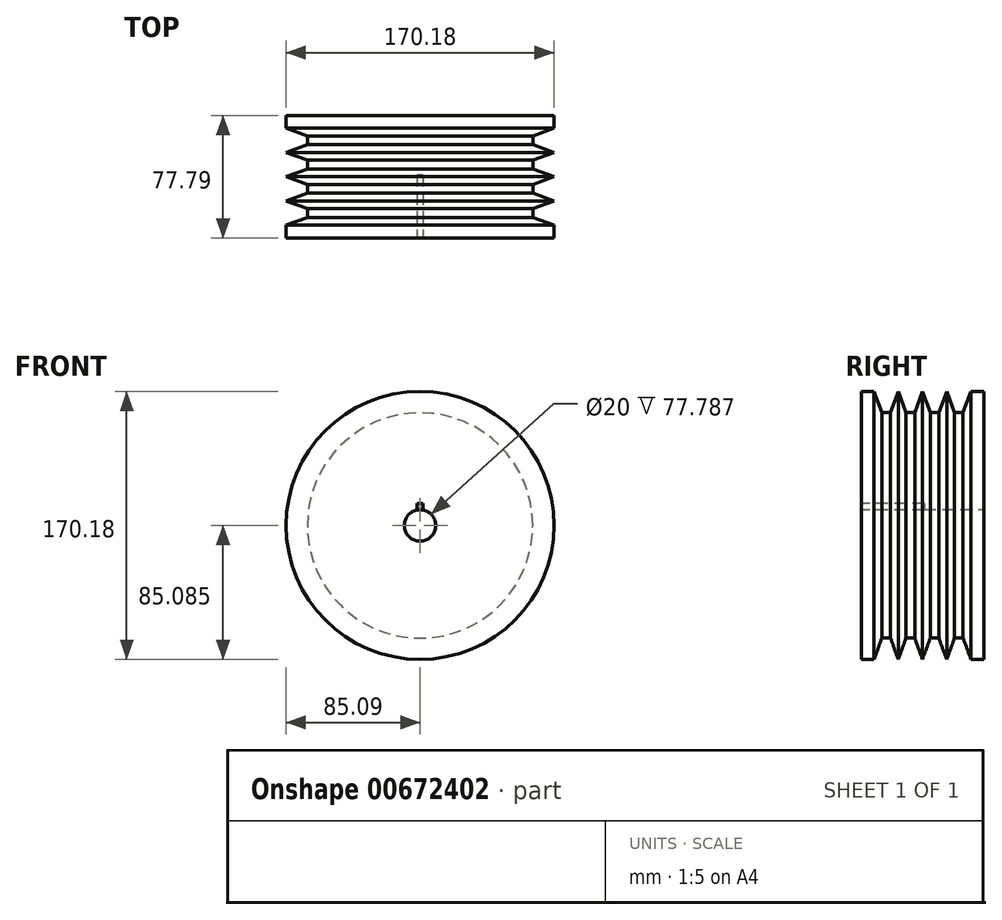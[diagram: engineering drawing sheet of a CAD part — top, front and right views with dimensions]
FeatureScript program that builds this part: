
annotation { "Feature Type Name" : "Feature", "Feature Type Description" : "" }
export const myFeature = defineFeature(function(context is Context, id is Id, definition is map)
    precondition{}
    {
        {
            var Q0;
            Q0=qCreatedBy(makeId("Right.planeOp"),FACE);
            var sketch = newSketch(context, id + "F0", { "sketchPlane" : qUnion([Q0])});
            skLineSegment(sketch, "E0.bottom", {"start": v(-37.93, 31.39) * mm, "end": v(-29.8, 31.39) * mm});
            skLineSegment(sketch, "E0.top", {"start": v(-37.93, -53.7) * mm, "end": v(39.86, -53.7) * mm});
            skLineSegment(sketch, "E0.left", {"start": v(-37.93, 31.39) * mm, "end": v(-37.93, -53.7) * mm});
            skLineSegment(sketch, "E0.right", {"start": v(39.86, 31.39) * mm, "end": v(39.86, -53.7) * mm});
            skPoint(sketch, "E0.middle", {"position": v(0.97, -11.16) * mm});
            skLineSegment(sketch, "E1.top", {"start": v(-29.8, -53.7) * mm, "end": v(31.73, -53.7) * mm});
            skLineSegment(sketch, "E2", {"start": v(-24.88, 17.9) * mm, "end": v(-19.32, 17.9) * mm});
            skLineSegment(sketch, "E3.direction1", {"start": v(-24.88, 17.9) * mm, "end": v(-19.32, 17.9) * mm, "construction": true});
            skLineSegment(sketch, "E4", {"start": v(-29.8, 31.39) * mm, "end": v(-24.88, 17.9) * mm});
            skLineSegment(sketch, "E5", {"start": v(-19.32, 17.9) * mm, "end": v(-14.41, 31.39) * mm});
            skLineSegment(sketch, "E6.1.0.0", {"start": v(-14.41, 31.39) * mm, "end": v(-9.5, 17.9) * mm});
            skLineSegment(sketch, "E6.1.0.1", {"start": v(-9.5, 17.9) * mm, "end": v(-3.94, 17.9) * mm, "construction": true});
            skLineSegment(sketch, "E6.1.0.2", {"start": v(-3.94, 17.9) * mm, "end": v(0.97, 31.39) * mm});
            skLineSegment(sketch, "E6.2.0.0", {"start": v(0.97, 31.39) * mm, "end": v(5.88, 17.9) * mm});
            skLineSegment(sketch, "E6.2.0.1", {"start": v(5.88, 17.9) * mm, "end": v(11.44, 17.9) * mm, "construction": true});
            skLineSegment(sketch, "E6.2.0.2", {"start": v(11.44, 17.9) * mm, "end": v(16.35, 31.39) * mm});
            skLineSegment(sketch, "E6.3.0.0", {"start": v(16.35, 31.39) * mm, "end": v(21.26, 17.9) * mm});
            skLineSegment(sketch, "E6.3.0.1", {"start": v(21.26, 17.9) * mm, "end": v(26.82, 17.9) * mm, "construction": true});
            skLineSegment(sketch, "E6.3.0.2", {"start": v(26.82, 17.9) * mm, "end": v(31.73, 31.39) * mm});
            skLineSegment(sketch, "E6.direction1", {"start": v(-24.88, 17.9) * mm, "end": v(-9.5, 17.9) * mm, "construction": true});
            skLineSegment(sketch, "E7", {"start": v(-9.5, 17.9) * mm, "end": v(-3.94, 17.9) * mm});
            skLineSegment(sketch, "E8", {"start": v(5.88, 17.9) * mm, "end": v(11.44, 17.9) * mm});
            skLineSegment(sketch, "E9", {"start": v(21.26, 17.9) * mm, "end": v(26.82, 17.9) * mm});
            skLineSegment(sketch, "E10.trimOffspring", {"start": v(31.73, 31.39) * mm, "end": v(39.86, 31.39) * mm});
            skSolve(sketch);
        }
        {
            var Q0;
            Q0=makeQuery(id+"F0.imprint","IMPRINT",FACE,{"disambiguationData":[TD([[makeQuery(id+"F0.imprint","IMPRINT",EDGE,{"derivedFrom":sQuery(id+"F0.wireOp",EDGE,"E0.bottom")}),-1.0]])]});
            var Q1;
            Q1=sQuery(id+"F0.wireOp",EDGE,"E1.top");
            revolve(context, id + "F1", {"entities" : qUnion([Q0]), "axis" : qUnion([Q1]), "revolveType" : RevolveType.FULL});
        }
        {
            var Q0;
            Q0=makeQuery(id+"F1.opRevolve","SWEPT_FACE",FACE,{"disambiguationData":[OSD([sQuery(id+"F0.wireOp",EDGE,"E0.right")])]});
            var sketch = newSketch(context, id + "F2", { "sketchPlane" : qUnion([Q0])});
            skCircle(sketch, "E11", {"center": v(0, -53.7) * mm, "radius": 10 * mm});
            skSolve(sketch);
        }
        {
            var Q0;
            Q0 = qSketchRegion(id + "F2", true);
            extrude(context, id + "F3", {"entities" : qUnion([Q0]), "operationType" : NewBodyOperationType.REMOVE, "oppositeDirection" : true, "depth" : 77.98 * mm, "offsetDistance" : 25.4 * mm});
        }
        {
            var Q0;
            Q0=makeQuery(id+"F1.opRevolve","SWEPT_FACE",FACE,{"disambiguationData":[OSD([sQuery(id+"F0.wireOp",EDGE,"E0.left")])]});
            var sketch = newSketch(context, id + "F4", { "sketchPlane" : qUnion([Q0])});
            skLineSegment(sketch, "E12", {"start": v(0, -39.7) * mm, "end": v(-2, -39.7) * mm});
            skLineSegment(sketch, "E13", {"start": v(-2, -39.7) * mm, "end": v(-2, -43.9) * mm});
            skLineSegment(sketch, "E14", {"start": v(2, -43.9) * mm, "end": v(2, -39.7) * mm});
            skLineSegment(sketch, "E15", {"start": v(2, -39.7) * mm, "end": v(0, -39.7) * mm});
            skSolve(sketch);
        }
        {
            var Q0;
            Q0 = qSketchRegion(id + "F4", true);
            var Q1;
            Q1=makeQuery(id+"F4.imprint","IMPRINT",FACE,{"disambiguationData":[TD([[makeQuery(id+"F4.imprint","IMPRINT",EDGE,{"derivedFrom":sQuery(id+"F4.wireOp",EDGE,"E12")}),1.0]])]});
            extrude(context, id + "F5", {"entities" : qUnion([Q0, Q1]), "operationType" : NewBodyOperationType.REMOVE, "oppositeDirection" : true, "depth" : 40 * mm, "offsetDistance" : 25.4 * mm});
        }
    });
